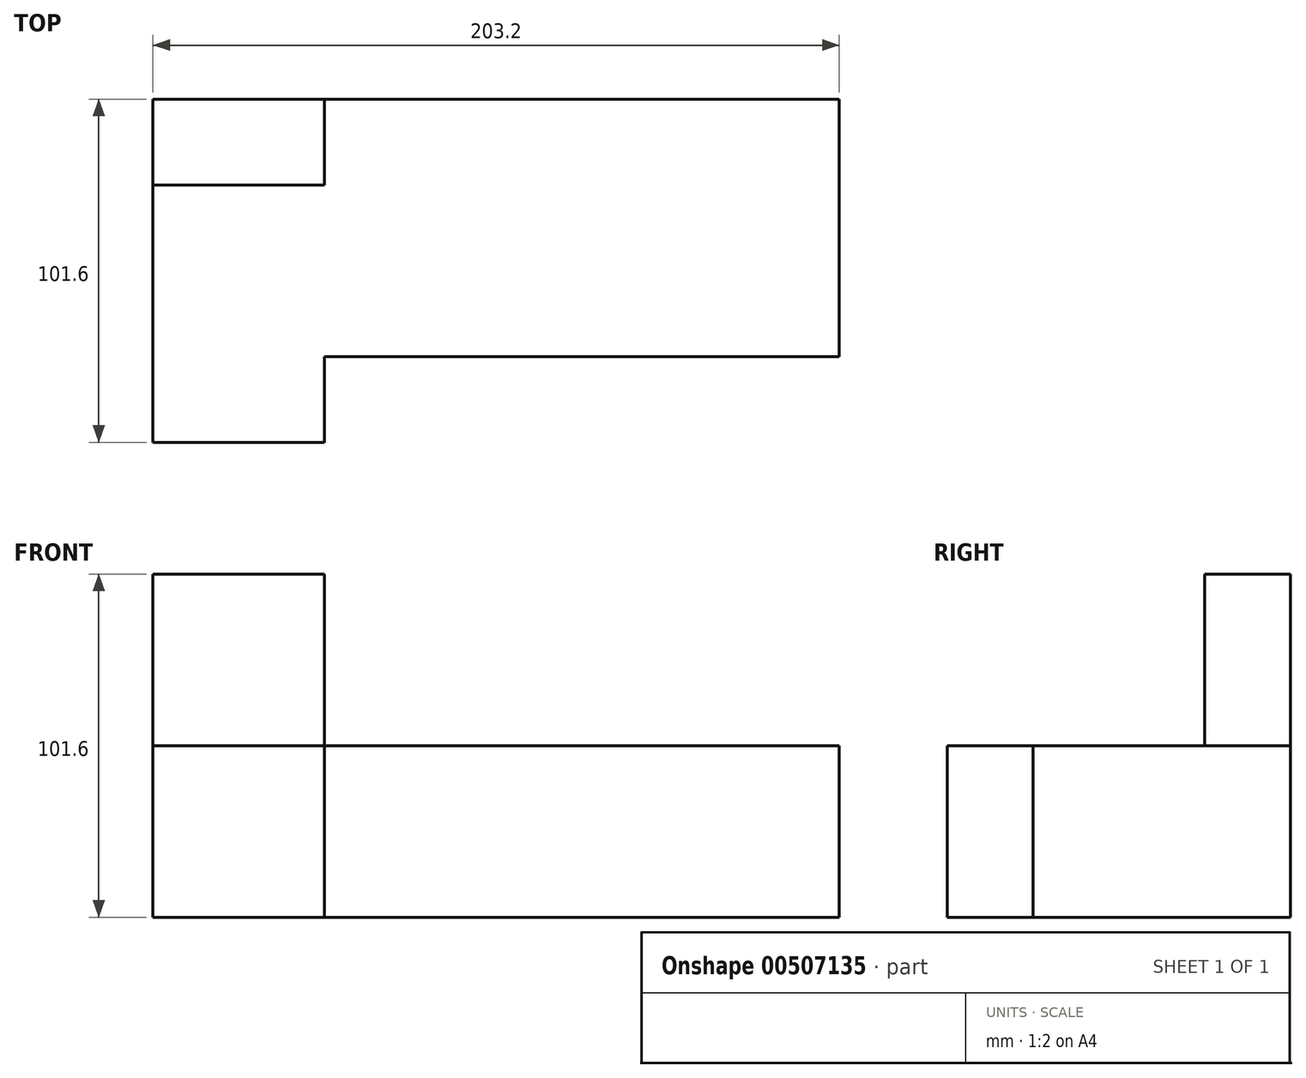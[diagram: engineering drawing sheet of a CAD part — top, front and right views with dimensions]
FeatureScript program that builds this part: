
annotation { "Feature Type Name" : "Feature", "Feature Type Description" : "" }
export const myFeature = defineFeature(function(context is Context, id is Id, definition is map)
    precondition{}
    {
        {
            var Q0;
            Q0=qCreatedBy(makeId("Top.planeOp"),FACE);
            var sketch = newSketch(context, id + "F0", { "sketchPlane" : qUnion([Q0])});
            skLineSegment(sketch, "E0.bottom", {"start": v(101.6, 50.8) * mm, "end": v(-101.6, 50.8) * mm});
            skLineSegment(sketch, "E0.top", {"start": v(101.6, -50.8) * mm, "end": v(-101.6, -50.8) * mm});
            skLineSegment(sketch, "E0.left", {"start": v(101.6, 50.8) * mm, "end": v(101.6, -50.8) * mm});
            skLineSegment(sketch, "E0.right", {"start": v(-101.6, 50.8) * mm, "end": v(-101.6, -50.8) * mm});
            skPoint(sketch, "E0.middle", {"position": v(0, 0) * mm});
            skLineSegment(sketch, "E1.bottom", {"start": v(101.6, -50.8) * mm, "end": v(-50.8, -50.8) * mm});
            skLineSegment(sketch, "E1.left", {"start": v(101.6, -50.8) * mm, "end": v(101.6, -25.4) * mm});
            skLineSegment(sketch, "E2.bottom", {"start": v(-50.8, -50.8) * mm, "end": v(101.6, -50.8) * mm});
            skSolve(sketch);
        }
        {
            var Q0;
            Q0 = qSketchRegion(id + "F0", true);
            extrude(context, id + "F1", {"entities" : qUnion([Q0]), "depth" : 50.8 * mm});
        }
        {
            var Q0;
            Q0=makeQuery(id+"F1.opExtrude","CAP_FACE",FACE,{"disambiguationData":[OSD([sQuery(id+"F0.wireOp",EDGE,"E0.bottom"),sQuery(id+"F0.wireOp",EDGE,"E0.top"),sQuery(id+"F0.wireOp",EDGE,"E0.left"),sQuery(id+"F0.wireOp",EDGE,"E0.right"),sQuery(id+"F0.wireOp",EDGE,"E2.bottom"),sQuery(id+"F0.wireOp",EDGE,"E1.left")])],"isStart":false});
            var sketch = newSketch(context, id + "F2", { "sketchPlane" : qUnion([Q0])});
            skLineSegment(sketch, "E3.bottom", {"start": v(101.6, -50.8) * mm, "end": v(-50.8, -50.8) * mm});
            skLineSegment(sketch, "E3.top", {"start": v(101.6, -25.4) * mm, "end": v(-50.8, -25.4) * mm});
            skLineSegment(sketch, "E3.left", {"start": v(101.6, -50.8) * mm, "end": v(101.6, -25.4) * mm});
            skLineSegment(sketch, "E3.right", {"start": v(-50.8, -50.8) * mm, "end": v(-50.8, -25.4) * mm});
            skSolve(sketch);
        }
        {
            var Q0;
            Q0=makeQuery(id+"F2.imprint","IMPRINT",FACE,{"disambiguationData":[TD([[makeQuery(id+"F2.imprint","IMPRINT",EDGE,{"derivedFrom":sQuery(id+"F2.wireOp",EDGE,"E3.bottom")}),-1.0]])]});
            extrude(context, id + "F3", {"entities" : qUnion([Q0]), "operationType" : NewBodyOperationType.REMOVE, "oppositeDirection" : true, "depth" : 50.8 * mm});
        }
        {
            var Q0;
            Q0=makeQuery(id+"F1.opExtrude","SWEPT_FACE",FACE,{"disambiguationData":[OSD([sQuery(id+"F0.wireOp",EDGE,"E0.right")])]});
            var sketch = newSketch(context, id + "F4", { "sketchPlane" : qUnion([Q0])});
            skLineSegment(sketch, "E4.bottom", {"start": v(-50.8, 50.8) * mm, "end": v(-25.4, 50.8) * mm});
            skLineSegment(sketch, "E4.top", {"start": v(-50.8, 101.6) * mm, "end": v(-25.4, 101.6) * mm});
            skLineSegment(sketch, "E4.left", {"start": v(-50.8, 50.8) * mm, "end": v(-50.8, 101.6) * mm});
            skLineSegment(sketch, "E4.right", {"start": v(-25.4, 50.8) * mm, "end": v(-25.4, 101.6) * mm});
            skSolve(sketch);
        }
        {
            var Q0;
            Q0=makeQuery(id+"F4.imprint","IMPRINT",FACE,{"disambiguationData":[TD([[makeQuery(id+"F4.imprint","IMPRINT",EDGE,{"derivedFrom":sQuery(id+"F4.wireOp",EDGE,"E4.bottom")}),1.0]])]});
            extrude(context, id + "F5", {"entities" : qUnion([Q0]), "operationType" : NewBodyOperationType.ADD, "oppositeDirection" : true, "depth" : 50.8 * mm});
        }
    });
